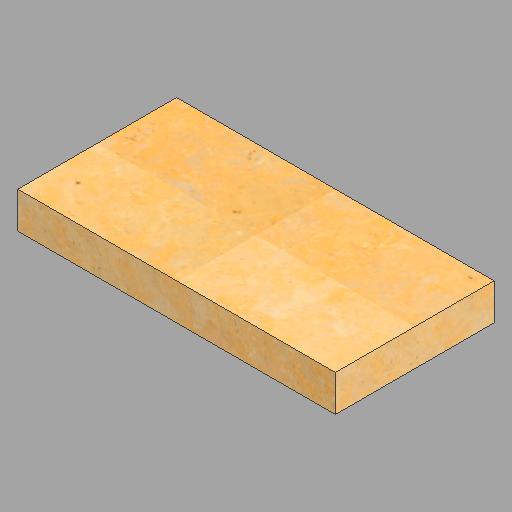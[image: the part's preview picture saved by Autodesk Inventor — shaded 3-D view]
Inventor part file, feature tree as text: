
AUTODESK INVENTOR PART (.ipt)
format: ipt  version: 2023 (Build 270158030, 158C)  size: 255,488 bytes
history: native  units: in
note: dims shown in document units (in); Inventor stores cm internally (conversion verified against a paired STEP export)
features: extrude x1, sketch x1
ambient origin geometry x8: Origin, YZ Plane, XZ Plane, XY Plane, X Axis, Y Axis, Z Axis, Center Point
bodies: Solid1 (feature_tree)
feature tree (2):
  extrude  "Extrusion1"  Depth=12.0in
  sketch  "Sketch1"  dims[d0=24.0in d1=12.0in d2=2.75in d3=0.0in]
